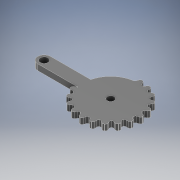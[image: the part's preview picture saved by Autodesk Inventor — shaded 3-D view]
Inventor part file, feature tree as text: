
AUTODESK INVENTOR PART (.ipt)
format: ipt  version: 2021 (Build 250183000, 183)  size: 251,392 bytes
history: native  units: mm
features: extrude x2, sketch x2, fillet x1, pattern_circular x1
ambient origin geometry x8: Origin, YZ Plane, XZ Plane, XY Plane, X Axis, Y Axis, Z Axis, Center Point
bodies: Solid1 (feature_tree)
feature tree (6):
  extrude  "Extrusion1"  Depth=20.0mm
  extrude  "Extrusion2"  Depth=1.0mm
  fillet  "Fillet1"  Radius=3.0mm
  pattern_circular  "Circular Pattern1"  [2 undecoded]
  sketch  "Sketch1"  dims[d0=27.5mm d1=20.0mm]
  sketch  "Sketch2"  dims[d2=6.5mm d3=3.5mm d4=3.0mm d5=0.0mm d6=2.25mm d7=1.65mm d8=1.5mm d9=3.0mm d10=0.0mm d11=1.0mm d12=150.0mm d13=43.633231mm d15=4.0mm]
note: 2 required parameter values undecoded (feature->parameter linkage not recoverable at this tier; creation-order binding heuristic only, values carry confidence <= 0.55)
